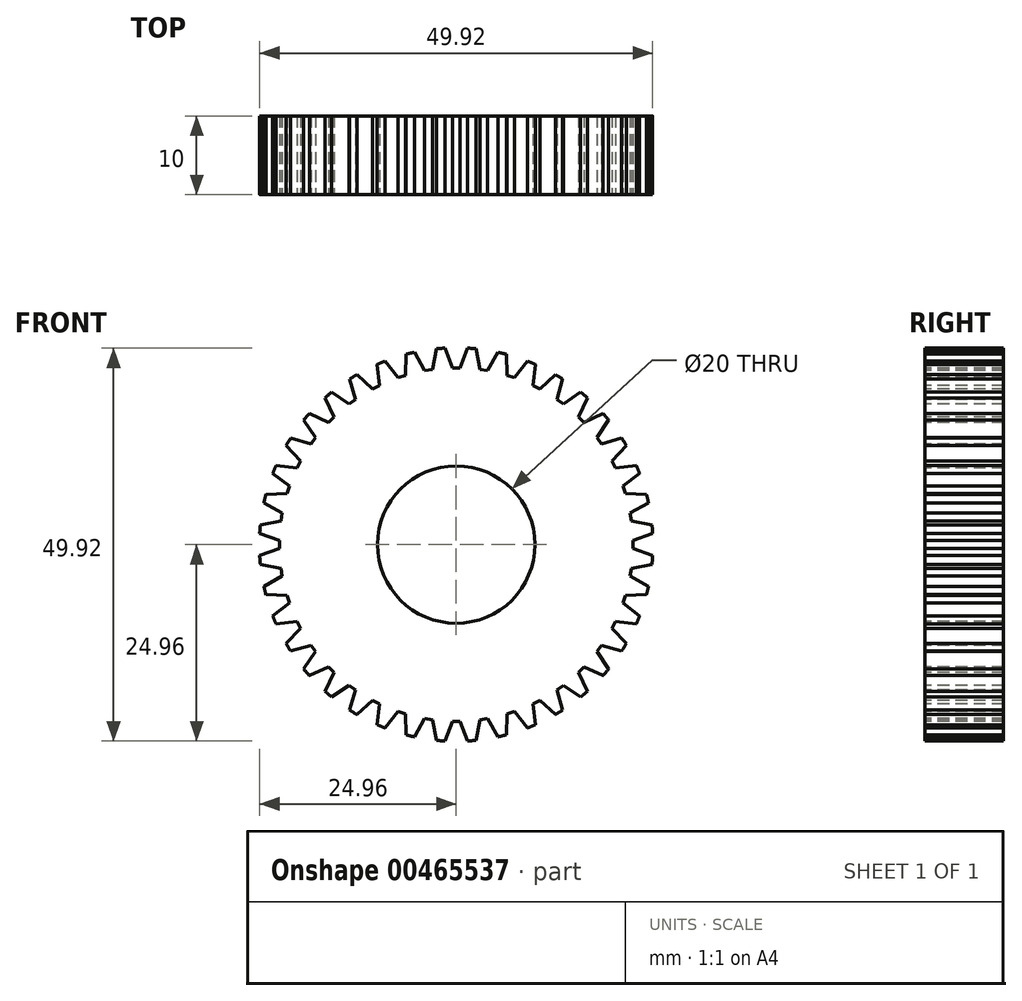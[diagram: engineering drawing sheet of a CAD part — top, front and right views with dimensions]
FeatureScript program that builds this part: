
annotation { "Feature Type Name" : "Feature", "Feature Type Description" : "" }
export const myFeature = defineFeature(function(context is Context, id is Id, definition is map)
    precondition{}
    {
        {
            var Q0;
            Q0=qCreatedBy(makeId("Front.planeOp"),FACE);
            var sketch = newSketch(context, id + "F0", { "sketchPlane" : qUnion([Q0])});
            skCircle(sketch, "E0", {"center": v(0, 0) * mm, "radius": 25 * mm});
            skCircle(sketch, "E1", {"center": v(0, 0) * mm, "radius": 10 * mm});
            skSolve(sketch);
        }
        {
            var Q0;
            Q0=makeQuery(id+"F0.imprint","IMPRINT",FACE,{"disambiguationData":[TD([[makeQuery(id+"F0.imprint","IMPRINT",EDGE,{"derivedFrom":sQuery(id+"F0.wireOp",EDGE,"E0")}),1.0]])]});
            extrude(context, id + "F1", {"entities" : qUnion([Q0]), "depth" : 10 * mm});
        }
        {
            var Q0;
            Q0=makeQuery(id+"F1.opExtrude","CAP_FACE",FACE,{"disambiguationData":[OSD([sQuery(id+"F0.wireOp",EDGE,"E0"),sQuery(id+"F0.wireOp",EDGE,"E1")])],"isStart":false});
            var sketch = newSketch(context, id + "F2", { "sketchPlane" : qUnion([Q0])});
            skLineSegment(sketch, "E2", {"start": v(0, 0) * mm, "end": v(0, 25) * mm, "construction": true});
            skLineSegment(sketch, "E3", {"start": v(0, 25) * mm, "end": v(0, 22.45) * mm, "construction": true});
            skLineSegment(sketch, "E4", {"start": v(0, 22.45) * mm, "end": v(-0.5, 22.45) * mm});
            skLineSegment(sketch, "E5", {"start": v(0, 22.45) * mm, "end": v(0.5, 22.45) * mm});
            skLineSegment(sketch, "E6", {"start": v(-0.5, 22.45) * mm, "end": v(-1.41, 24.96) * mm});
            skLineSegment(sketch, "E7", {"start": v(0.5, 22.45) * mm, "end": v(1.41, 24.96) * mm});
            skSolve(sketch);
        }
        {
            var Q0;
            Q0=makeQuery(id+"F2.imprint","IMPRINT",FACE,{"disambiguationData":[TD([[makeQuery(id+"F2.imprint","IMPRINT",EDGE,{"derivedFrom":sQuery(id+"F2.wireOp",EDGE,"E4")}),-1.0]])]});
            extrude(context, id + "F3", {"entities" : qUnion([Q0]), "operationType" : NewBodyOperationType.REMOVE, "oppositeDirection" : true, "depth" : 25 * mm});
        }
        {
            var Q0;
            Q0=makeQuery(id+"F3.boolean.opBoolean","COPY",FACE,{"derivedFrom":makeQuery(id+"F3.opExtrude","SWEPT_FACE",FACE,{"disambiguationData":[OSD([sQuery(id+"F2.wireOp",EDGE,"E6")])]})});
            var Q1;
            Q1=makeQuery(id+"F3.boolean.opBoolean","COPY",FACE,{"derivedFrom":makeQuery(id+"F3.opExtrude","SWEPT_FACE",FACE,{"disambiguationData":[OSD([sQuery(id+"F2.wireOp",EDGE,"E4"),sQuery(id+"F2.wireOp",EDGE,"E5")])]})});
            var Q2;
            Q2=makeQuery(id+"F3.boolean.opBoolean","COPY",FACE,{"derivedFrom":makeQuery(id+"F3.opExtrude","SWEPT_FACE",FACE,{"disambiguationData":[OSD([sQuery(id+"F2.wireOp",EDGE,"E7")])]})});
            var Q3;
            Q3=makeQuery(id+"F1.opExtrude","SWEPT_FACE",FACE,{"disambiguationData":[OSD([sQuery(id+"F0.wireOp",EDGE,"E0")])]});
            circularPattern(context, id + "F4", {"patternType" : PatternType.FACE, "faces" : qUnion([Q0, Q1, Q2]), "axis" : qUnion([Q3]), "angle" : 360 * degree, "instanceCount" : 40, "equalSpace" : true});
        }
    });
